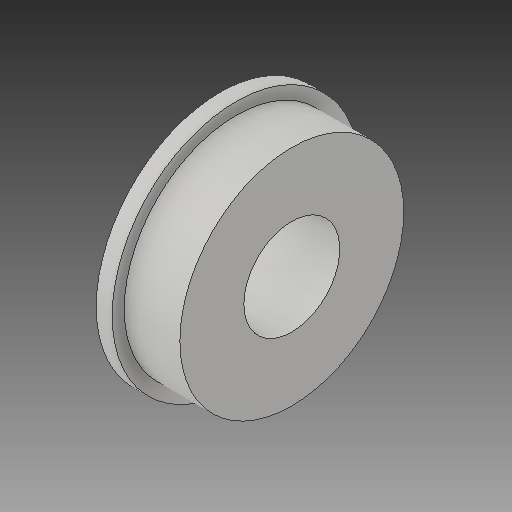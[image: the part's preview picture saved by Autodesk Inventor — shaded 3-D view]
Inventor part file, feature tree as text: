
AUTODESK INVENTOR PART (.ipt)
format: ipt  version: 2018 (Build 220112000, 112)  size: 128,512 bytes
history: native  units: in
note: dims shown in document units (in); Inventor stores cm internally (conversion verified against a paired STEP export)
features: revolve x1
ambient origin geometry x8: Origin, YZ Plane, XZ Plane, XY Plane, X Axis, Y Axis, Z Axis, Center Point
bodies: Solid1 (feature_tree)
feature tree (1):
  revolve  "Revolve1"  [1 undecoded]
note: 1 required parameter value undecoded (feature->parameter linkage not recoverable at this tier; creation-order binding heuristic only, values carry confidence <= 0.55)
